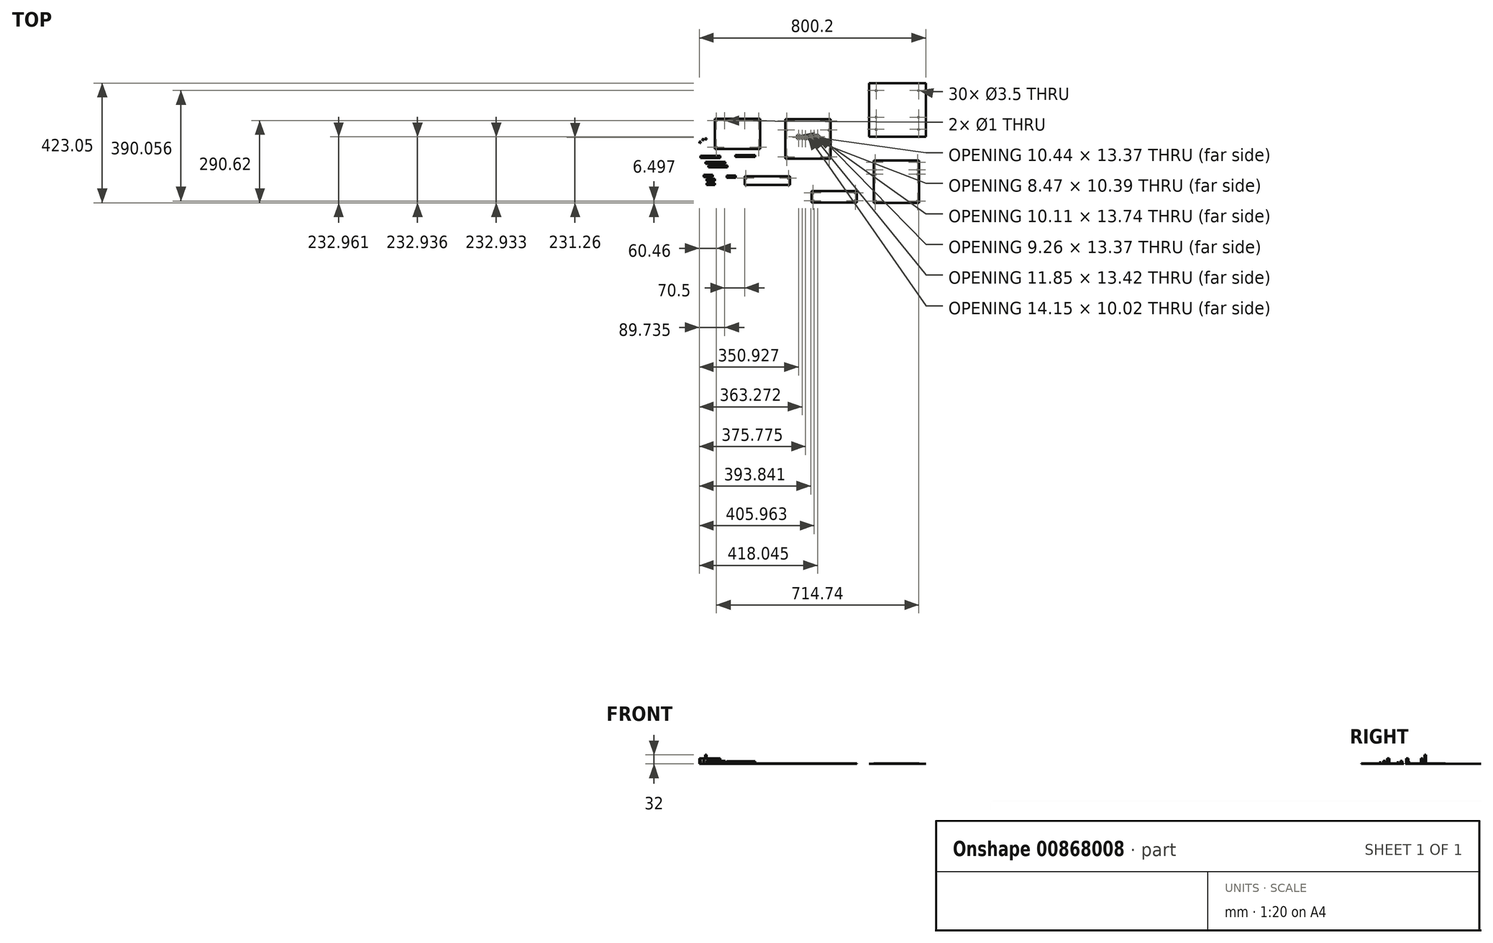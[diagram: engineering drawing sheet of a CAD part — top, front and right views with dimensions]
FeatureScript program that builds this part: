
annotation { "Feature Type Name" : "Feature", "Feature Type Description" : "" }
export const myFeature = defineFeature(function(context is Context, id is Id, definition is map)
    precondition{}
    {
        {
            var Q0;
            Q0=qCreatedBy(makeId("Top.planeOp"),FACE);
            var sketch = newSketch(context, id + "F0", { "sketchPlane" : qUnion([Q0])});
            skLineSegment(sketch, "E0.bottom", {"start": v(0, 0) * mm, "end": v(160, 0) * mm});
            skLineSegment(sketch, "E0.top", {"start": v(0, 107.5) * mm, "end": v(160, 107.5) * mm});
            skLineSegment(sketch, "E0.left", {"start": v(0, 0) * mm, "end": v(0, 107.5) * mm});
            skLineSegment(sketch, "E0.right", {"start": v(160, 0) * mm, "end": v(160, 107.5) * mm});
            skLineSegment(sketch, "E1", {"start": v(34.27, 115.15) * mm, "end": v(34.27, 89.45) * mm, "construction": true});
            skLineSegment(sketch, "E2", {"start": v(104.78, 115.15) * mm, "end": v(104.78, 86.57) * mm, "construction": true});
            skLineSegment(sketch, "E3.bottom", {"start": v(5, 101) * mm, "end": v(155, 101) * mm, "construction": true});
            skLineSegment(sketch, "E3.top", {"start": v(5, 6.5) * mm, "end": v(155, 6.5) * mm, "construction": true});
            skLineSegment(sketch, "E3.left", {"start": v(5, 101) * mm, "end": v(5, 6.5) * mm, "construction": true});
            skLineSegment(sketch, "E3.right", {"start": v(155, 101) * mm, "end": v(155, 6.5) * mm, "construction": true});
            skCircle(sketch, "E4", {"center": v(34.27, 101) * mm, "radius": 0.5 * mm});
            skCircle(sketch, "E5", {"center": v(104.78, 101) * mm, "radius": 0.5 * mm});
            skSolve(sketch);
        }
        {
            var Q0;
            Q0=makeQuery(id+"F0.imprint","IMPRINT",FACE,{"disambiguationData":[TD([[makeQuery(id+"F0.imprint","IMPRINT",EDGE,{"derivedFrom":sQuery(id+"F0.wireOp",EDGE,"E0.bottom")}),1.0]])]});
            extrude(context, id + "F1", {"entities" : qUnion([Q0]), "depth" : 1.6 * mm, "offsetDistance" : 25 * mm});
        }
        {
            var Q0;
            Q0=sQuery(id+"F0.wireOp",VERTEX,"E3.bottom.start");
            var Q1;
            Q1=sQuery(id+"F0.wireOp",VERTEX,"E3.bottom.end");
            var Q2;
            Q2=sQuery(id+"F0.wireOp",VERTEX,"E3.top.end");
            var Q3;
            Q3=sQuery(id+"F0.wireOp",VERTEX,"E3.top.start");
            var Q4;
            Q4=makeQuery(id+"F1.opExtrude","SWEPT_BODY",BODY,{"disambiguationData":[OSD([sQuery(id+"F0.wireOp",EDGE,"E0.bottom"),sQuery(id+"F0.wireOp",EDGE,"E0.top"),sQuery(id+"F0.wireOp",EDGE,"E0.left"),sQuery(id+"F0.wireOp",EDGE,"E0.right")])]});
            hole(context, id + "F2", {"style" : HoleStyle.SIMPLE, "endStyle" : HoleEndStyle.THROUGH, "oppositeDirection" : true, "holeDiameter" : 3.5 * mm, "majorDiameter" : 5 * mm, "isTappedThrough" : true, "tappedDepth" : 12 * mm, "tapClearance" : 3, "startFromSketch" : true, "locations" : qUnion([Q0, Q1, Q2, Q3]), "scope" : qUnion([Q4])});
        }
        {
            var Q0;
            Q0=qCreatedBy(makeId("Top.planeOp"),FACE);
            var sketch = newSketch(context, id + "F3", { "sketchPlane" : qUnion([Q0])});
            skLineSegment(sketch, "E6.bottom", {"start": v(-51.1, -23.64) * mm, "end": v(18.9, -23.64) * mm});
            skLineSegment(sketch, "E6.top", {"start": v(-51.1, -30.64) * mm, "end": v(18.9, -30.64) * mm});
            skLineSegment(sketch, "E6.left", {"start": v(-51.1, -23.64) * mm, "end": v(-51.1, -30.64) * mm});
            skLineSegment(sketch, "E6.right", {"start": v(18.9, -23.64) * mm, "end": v(18.9, -30.64) * mm});
            skSolve(sketch);
        }
        {
            var Q0;
            Q0=makeQuery(id+"F3.imprint","IMPRINT",FACE,{"disambiguationData":[TD([[makeQuery(id+"F3.imprint","IMPRINT",EDGE,{"derivedFrom":sQuery(id+"F3.wireOp",EDGE,"E6.bottom")}),-1.0]])]});
            extrude(context, id + "F4", {"entities" : qUnion([Q0]), "depth" : 20 * mm, "offsetDistance" : 25 * mm});
        }
        {
            var Q0;
            Q0=qCreatedBy(makeId("Top.planeOp"),FACE);
            var sketch = newSketch(context, id + "F5", { "sketchPlane" : qUnion([Q0])});
            skLineSegment(sketch, "E7.bottom", {"start": v(-33.26, -44.66) * mm, "end": v(36.74, -44.66) * mm});
            skLineSegment(sketch, "E7.top", {"start": v(-33.26, -51.66) * mm, "end": v(36.74, -51.66) * mm});
            skLineSegment(sketch, "E7.left", {"start": v(-33.26, -44.66) * mm, "end": v(-33.26, -51.66) * mm});
            skLineSegment(sketch, "E7.right", {"start": v(36.74, -44.66) * mm, "end": v(36.74, -51.66) * mm});
            skSolve(sketch);
        }
        {
            var Q0;
            Q0=makeQuery(id+"F5.imprint","IMPRINT",FACE,{"disambiguationData":[TD([[makeQuery(id+"F5.imprint","IMPRINT",EDGE,{"derivedFrom":sQuery(id+"F5.wireOp",EDGE,"E7.bottom")}),-1.0]])]});
            extrude(context, id + "F6", {"entities" : qUnion([Q0]), "depth" : 10.4 * mm, "offsetDistance" : 25 * mm});
        }
        {
            var Q0;
            Q0=qCreatedBy(makeId("Top.planeOp"),FACE);
            var sketch = newSketch(context, id + "F7", { "sketchPlane" : qUnion([Q0])});
            skLineSegment(sketch, "E8.bottom", {"start": v(-22.8, -58.18) * mm, "end": v(44.2, -58.18) * mm});
            skLineSegment(sketch, "E8.top", {"start": v(-22.8, -63.88) * mm, "end": v(44.2, -63.88) * mm});
            skLineSegment(sketch, "E8.left", {"start": v(-22.8, -58.18) * mm, "end": v(-22.8, -63.88) * mm});
            skLineSegment(sketch, "E8.right", {"start": v(44.2, -58.18) * mm, "end": v(44.2, -63.88) * mm});
            skSolve(sketch);
        }
        {
            var Q0;
            Q0=makeQuery(id+"F7.imprint","IMPRINT",FACE,{"disambiguationData":[TD([[makeQuery(id+"F7.imprint","IMPRINT",EDGE,{"derivedFrom":sQuery(id+"F7.wireOp",EDGE,"E8.bottom")}),-1.0]])]});
            extrude(context, id + "F8", {"entities" : qUnion([Q0]), "depth" : 5.5 * mm, "offsetDistance" : 25 * mm});
        }
        {
            var Q0;
            Q0=qCreatedBy(makeId("Top.planeOp"),FACE);
            var sketch = newSketch(context, id + "F9", { "sketchPlane" : qUnion([Q0])});
            skLineSegment(sketch, "E9.bottom", {"start": v(72.56, -20.42) * mm, "end": v(142.56, -20.42) * mm});
            skLineSegment(sketch, "E9.top", {"start": v(72.56, -27.42) * mm, "end": v(142.56, -27.42) * mm});
            skLineSegment(sketch, "E9.left", {"start": v(72.56, -20.42) * mm, "end": v(72.56, -27.42) * mm});
            skLineSegment(sketch, "E9.right", {"start": v(142.56, -20.42) * mm, "end": v(142.56, -27.42) * mm});
            skSolve(sketch);
        }
        {
            var Q0;
            Q0=makeQuery(id+"F9.imprint","IMPRINT",FACE,{"disambiguationData":[TD([[makeQuery(id+"F9.imprint","IMPRINT",EDGE,{"derivedFrom":sQuery(id+"F9.wireOp",EDGE,"E9.bottom")}),-1.0]])]});
            extrude(context, id + "F10", {"entities" : qUnion([Q0]), "depth" : 9.8 * mm, "offsetDistance" : 25 * mm});
        }
        {
            var Q0;
            Q0=qCreatedBy(makeId("Top.planeOp"),FACE);
            var sketch = newSketch(context, id + "F11", { "sketchPlane" : qUnion([Q0])});
            skLineSegment(sketch, "E10.bottom", {"start": v(-40, -91.42) * mm, "end": v(-8, -91.42) * mm});
            skLineSegment(sketch, "E10.top", {"start": v(-40, -98.42) * mm, "end": v(-8, -98.42) * mm});
            skLineSegment(sketch, "E10.left", {"start": v(-40, -91.42) * mm, "end": v(-40, -98.42) * mm});
            skLineSegment(sketch, "E10.right", {"start": v(-8, -91.42) * mm, "end": v(-8, -98.42) * mm});
            skSolve(sketch);
        }
        {
            var Q0;
            Q0=makeQuery(id+"F11.imprint","IMPRINT",FACE,{"disambiguationData":[TD([[makeQuery(id+"F11.imprint","IMPRINT",EDGE,{"derivedFrom":sQuery(id+"F11.wireOp",EDGE,"E10.bottom")}),-1.0]])]});
            extrude(context, id + "F12", {"entities" : qUnion([Q0]), "depth" : 20 * mm, "offsetDistance" : 25 * mm});
        }
        {
            var Q0;
            Q0=qCreatedBy(makeId("Top.planeOp"),FACE);
            var sketch = newSketch(context, id + "F13", { "sketchPlane" : qUnion([Q0])});
            skLineSegment(sketch, "E11.bottom", {"start": v(-30, -105.14) * mm, "end": v(0, -105.14) * mm});
            skLineSegment(sketch, "E11.top", {"start": v(-30, -112.14) * mm, "end": v(0, -112.14) * mm});
            skLineSegment(sketch, "E11.left", {"start": v(-30, -105.14) * mm, "end": v(-30, -112.14) * mm});
            skLineSegment(sketch, "E11.right", {"start": v(0, -105.14) * mm, "end": v(0, -112.14) * mm});
            skSolve(sketch);
        }
        {
            var Q0;
            Q0=makeQuery(id+"F13.imprint","IMPRINT",FACE,{"disambiguationData":[TD([[makeQuery(id+"F13.imprint","IMPRINT",EDGE,{"derivedFrom":sQuery(id+"F13.wireOp",EDGE,"E11.bottom")}),-1.0]])]});
            extrude(context, id + "F14", {"entities" : qUnion([Q0]), "depth" : 10.4 * mm, "offsetDistance" : 25 * mm});
        }
        {
            var Q0;
            Q0=qCreatedBy(makeId("Top.planeOp"),FACE);
            var sketch = newSketch(context, id + "F15", { "sketchPlane" : qUnion([Q0])});
            skLineSegment(sketch, "E12.bottom", {"start": v(-29, -120.64) * mm, "end": v(0, -120.64) * mm});
            skLineSegment(sketch, "E12.top", {"start": v(-29, -126.34) * mm, "end": v(0, -126.34) * mm});
            skLineSegment(sketch, "E12.left", {"start": v(-29, -120.64) * mm, "end": v(-29, -126.34) * mm});
            skLineSegment(sketch, "E12.right", {"start": v(0, -120.64) * mm, "end": v(0, -126.34) * mm});
            skSolve(sketch);
        }
        {
            var Q0;
            Q0=makeQuery(id+"F15.imprint","IMPRINT",FACE,{"disambiguationData":[TD([[makeQuery(id+"F15.imprint","IMPRINT",EDGE,{"derivedFrom":sQuery(id+"F15.wireOp",EDGE,"E12.bottom")}),-1.0]])]});
            extrude(context, id + "F16", {"entities" : qUnion([Q0]), "depth" : 5.5 * mm, "offsetDistance" : 25 * mm});
        }
        {
            var Q0;
            Q0=qCreatedBy(makeId("Top.planeOp"),FACE);
            var sketch = newSketch(context, id + "F17", { "sketchPlane" : qUnion([Q0])});
            skLineSegment(sketch, "E13.bottom", {"start": v(41.03, -93.71) * mm, "end": v(73.03, -93.71) * mm});
            skLineSegment(sketch, "E13.top", {"start": v(41.03, -100.71) * mm, "end": v(73.03, -100.71) * mm});
            skLineSegment(sketch, "E13.left", {"start": v(41.03, -93.71) * mm, "end": v(41.03, -100.71) * mm});
            skLineSegment(sketch, "E13.right", {"start": v(73.03, -93.71) * mm, "end": v(73.03, -100.71) * mm});
            skSolve(sketch);
        }
        {
            var Q0;
            Q0=makeQuery(id+"F17.imprint","IMPRINT",FACE,{"disambiguationData":[TD([[makeQuery(id+"F17.imprint","IMPRINT",EDGE,{"derivedFrom":sQuery(id+"F17.wireOp",EDGE,"E13.bottom")}),-1.0]])]});
            extrude(context, id + "F18", {"entities" : qUnion([Q0]), "depth" : 9.8 * mm, "offsetDistance" : 25 * mm});
        }
        {
            var Q0;
            Q0=qCreatedBy(makeId("Top.planeOp"),FACE);
            var sketch = newSketch(context, id + "F19", { "sketchPlane" : qUnion([Q0])});
            skCircle(sketch, "E14.cCircle", {"center": v(-52.9, 24.26) * mm, "radius": 2.5 * mm, "construction": true});
            skLineSegment(sketch, "E14.0", {"start": v(-52.82, 27.15) * mm, "end": v(-50.36, 25.63) * mm});
            skLineSegment(sketch, "E14.1", {"start": v(-50.36, 25.63) * mm, "end": v(-50.46, 22.74) * mm});
            skLineSegment(sketch, "E14.2", {"start": v(-50.46, 22.74) * mm, "end": v(-53, 21.38) * mm});
            skLineSegment(sketch, "E14.3", {"start": v(-53, 21.38) * mm, "end": v(-55.46, 22.9) * mm});
            skLineSegment(sketch, "E14.4", {"start": v(-55.46, 22.9) * mm, "end": v(-55.36, 25.79) * mm});
            skLineSegment(sketch, "E14.5", {"start": v(-55.36, 25.79) * mm, "end": v(-52.82, 27.15) * mm});
            skPoint(sketch, "E14.0.midPoint", {"position": v(-51.59, 26.39) * mm});
            skSolve(sketch);
        }
        {
            var Q0;
            Q0=makeQuery(id+"F19.imprint","IMPRINT",FACE,{"disambiguationData":[TD([[makeQuery(id+"F19.imprint","IMPRINT",EDGE,{"derivedFrom":sQuery(id+"F19.wireOp",EDGE,"E14.0")}),-1.0]])]});
            extrude(context, id + "F20", {"entities" : qUnion([Q0]), "depth" : 20 * mm, "offsetDistance" : 25 * mm});
        }
        {
            var Q0;
            Q0=qCreatedBy(makeId("Top.planeOp"),FACE);
            var sketch = newSketch(context, id + "F21", { "sketchPlane" : qUnion([Q0])});
            skLineSegment(sketch, "E15.bottom", {"start": v(104.6, -96.45) * mm, "end": v(264.6, -96.45) * mm});
            skLineSegment(sketch, "E15.top", {"start": v(104.6, -126.45) * mm, "end": v(264.6, -126.45) * mm});
            skLineSegment(sketch, "E15.left", {"start": v(104.6, -96.45) * mm, "end": v(104.6, -126.45) * mm});
            skLineSegment(sketch, "E15.right", {"start": v(264.6, -96.45) * mm, "end": v(264.6, -126.45) * mm});
            skCircle(sketch, "E16", {"center": v(109.6, -102.95) * mm, "radius": 1.75 * mm});
            skCircle(sketch, "E17", {"center": v(259.6, -102.95) * mm, "radius": 1.75 * mm});
            skSolve(sketch);
        }
        {
            var Q0;
            Q0=makeQuery(id+"F21.imprint","IMPRINT",FACE,{"disambiguationData":[TD([[makeQuery(id+"F21.imprint","IMPRINT",EDGE,{"derivedFrom":sQuery(id+"F21.wireOp",EDGE,"E15.bottom")}),-1.0]])]});
            extrude(context, id + "F22", {"entities" : qUnion([Q0]), "depth" : 1.6 * mm, "offsetDistance" : 25 * mm});
        }
        {
            var Q0;
            Q0=qCreatedBy(makeId("Top.planeOp"),FACE);
            var sketch = newSketch(context, id + "F23", { "sketchPlane" : qUnion([Q0])});
            skLineSegment(sketch, "E18.bottom", {"start": v(248.41, 106.6) * mm, "end": v(408.41, 106.6) * mm});
            skLineSegment(sketch, "E18.top", {"start": v(248.41, -33.4) * mm, "end": v(408.41, -33.4) * mm});
            skLineSegment(sketch, "E18.left", {"start": v(248.41, 106.6) * mm, "end": v(248.41, -33.4) * mm});
            skLineSegment(sketch, "E18.right", {"start": v(408.41, 106.6) * mm, "end": v(408.41, -33.4) * mm});
            skCircle(sketch, "E19", {"center": v(253.41, 100.1) * mm, "radius": 1.75 * mm});
            skCircle(sketch, "E20", {"center": v(403.41, 100.1) * mm, "radius": 1.75 * mm});
            skCircle(sketch, "E21", {"center": v(253.41, 67.6) * mm, "radius": 1.75 * mm});
            skCircle(sketch, "E22", {"center": v(403.41, 67.6) * mm, "radius": 1.75 * mm});
            skCircle(sketch, "E23", {"center": v(253.41, -26.9) * mm, "radius": 1.75 * mm});
            skCircle(sketch, "E24", {"center": v(403.41, -26.9) * mm, "radius": 1.75 * mm});
            skText(sketch, "E25", { "text": "New ACB", "fontName": "OpenSans-Regular.ttf"});
            const initialGuessF23  = {"E25": [0.28841, 0.03663, 1, 0, 0.01348]};
            skSetInitialGuess(sketch, initialGuessF23);
            skSolve(sketch);
        }
        {
            var Q0;
            Q0=makeQuery(id+"F23.imprint","IMPRINT",FACE,{"disambiguationData":[TD([[makeQuery(id+"F23.imprint","IMPRINT",EDGE,{"derivedFrom":sQuery(id+"F23.wireOp",EDGE,"E18.bottom")}),-1.0]])]});
            extrude(context, id + "F24", {"entities" : qUnion([Q0]), "depth" : 1.6 * mm, "offsetDistance" : 25 * mm});
        }
        {
            var Q0;
            Q0=qCreatedBy(makeId("Top.planeOp"),FACE);
            var sketch = newSketch(context, id + "F25", { "sketchPlane" : qUnion([Q0])});
            skCircle(sketch, "E26.cCircle", {"center": v(-41.73, 33.8) * mm, "radius": 2.5 * mm, "construction": true});
            skLineSegment(sketch, "E26.0", {"start": v(-39.25, 32.34) * mm, "end": v(-41.76, 30.91) * mm});
            skLineSegment(sketch, "E26.1", {"start": v(-41.76, 30.91) * mm, "end": v(-44.25, 32.38) * mm});
            skLineSegment(sketch, "E26.2", {"start": v(-44.25, 32.38) * mm, "end": v(-44.22, 35.26) * mm});
            skLineSegment(sketch, "E26.3", {"start": v(-44.22, 35.26) * mm, "end": v(-41.71, 36.69) * mm});
            skLineSegment(sketch, "E26.4", {"start": v(-41.71, 36.69) * mm, "end": v(-39.22, 35.22) * mm});
            skLineSegment(sketch, "E26.5", {"start": v(-39.22, 35.22) * mm, "end": v(-39.25, 32.34) * mm});
            skPoint(sketch, "E26.0.midPoint", {"position": v(-40.5, 31.63) * mm});
            skSolve(sketch);
        }
        {
            var Q0;
            Q0=makeQuery(id+"F25.imprint","IMPRINT",FACE,{"disambiguationData":[TD([[makeQuery(id+"F25.imprint","IMPRINT",EDGE,{"derivedFrom":sQuery(id+"F25.wireOp",EDGE,"E26.0")}),-1.0]])]});
            extrude(context, id + "F26", {"entities" : qUnion([Q0]), "depth" : 10 * mm, "offsetDistance" : 25 * mm});
        }
        {
            var Q0;
            Q0=qCreatedBy(makeId("Top.planeOp"),FACE);
            var sketch = newSketch(context, id + "F27", { "sketchPlane" : qUnion([Q0])});
            skCircle(sketch, "E27.cCircle", {"center": v(-32.14, 35.9) * mm, "radius": 2.5 * mm, "construction": true});
            skLineSegment(sketch, "E27.0", {"start": v(-29.63, 34.48) * mm, "end": v(-32.12, 33.02) * mm});
            skLineSegment(sketch, "E27.1", {"start": v(-32.12, 33.02) * mm, "end": v(-34.63, 34.45) * mm});
            skLineSegment(sketch, "E27.2", {"start": v(-34.63, 34.45) * mm, "end": v(-34.65, 37.33) * mm});
            skLineSegment(sketch, "E27.3", {"start": v(-34.65, 37.33) * mm, "end": v(-32.15, 38.8) * mm});
            skLineSegment(sketch, "E27.4", {"start": v(-32.15, 38.8) * mm, "end": v(-29.65, 37.36) * mm});
            skLineSegment(sketch, "E27.5", {"start": v(-29.65, 37.36) * mm, "end": v(-29.63, 34.48) * mm});
            skPoint(sketch, "E27.0.midPoint", {"position": v(-30.88, 33.75) * mm});
            skSolve(sketch);
        }
        {
            var Q0;
            Q0=makeQuery(id+"F27.imprint","IMPRINT",FACE,{"disambiguationData":[TD([[makeQuery(id+"F27.imprint","IMPRINT",EDGE,{"derivedFrom":sQuery(id+"F27.wireOp",EDGE,"E27.0")}),-1.0]])]});
            extrude(context, id + "F28", {"entities" : qUnion([Q0]), "depth" : 32 * mm, "offsetDistance" : 25 * mm});
        }
        {
            var Q0;
            Q0=qCreatedBy(makeId("Top.planeOp"),FACE);
            var sketch = newSketch(context, id + "F29", { "sketchPlane" : qUnion([Q0])});
            skLineSegment(sketch, "E28.bottom", {"start": v(341.16, -148.37) * mm, "end": v(501.16, -148.37) * mm});
            skLineSegment(sketch, "E28.top", {"start": v(341.16, -188.37) * mm, "end": v(501.16, -188.37) * mm});
            skLineSegment(sketch, "E28.left", {"start": v(341.16, -148.37) * mm, "end": v(341.16, -188.37) * mm});
            skLineSegment(sketch, "E28.right", {"start": v(501.16, -148.37) * mm, "end": v(501.16, -188.37) * mm});
            skCircle(sketch, "E29", {"center": v(346.16, -154.87) * mm, "radius": 1.75 * mm});
            skCircle(sketch, "E30", {"center": v(346.16, -181.87) * mm, "radius": 1.75 * mm});
            skCircle(sketch, "E31", {"center": v(496.16, -154.87) * mm, "radius": 1.75 * mm});
            skCircle(sketch, "E32", {"center": v(496.16, -181.87) * mm, "radius": 1.75 * mm});
            skSolve(sketch);
        }
        {
            var Q0;
            Q0=qCreatedBy(makeId("Top.planeOp"),FACE);
            var sketch = newSketch(context, id + "F30", { "sketchPlane" : qUnion([Q0])});
            skLineSegment(sketch, "E33.bottom", {"start": v(561.3, -39.62) * mm, "end": v(721.3, -39.62) * mm});
            skLineSegment(sketch, "E33.top", {"start": v(561.3, -189.62) * mm, "end": v(721.3, -189.62) * mm});
            skLineSegment(sketch, "E33.left", {"start": v(561.3, -39.62) * mm, "end": v(561.3, -189.62) * mm});
            skLineSegment(sketch, "E33.right", {"start": v(721.3, -39.62) * mm, "end": v(721.3, -189.62) * mm});
            skCircle(sketch, "E34", {"center": v(566.3, -183.12) * mm, "radius": 1.75 * mm});
            skCircle(sketch, "E35", {"center": v(716.3, -183.12) * mm, "radius": 1.75 * mm});
            skCircle(sketch, "E36", {"center": v(566.3, -88.62) * mm, "radius": 1.75 * mm});
            skCircle(sketch, "E37", {"center": v(716.3, -88.62) * mm, "radius": 1.75 * mm});
            skCircle(sketch, "E38", {"center": v(566.3, -73.12) * mm, "radius": 1.75 * mm});
            skCircle(sketch, "E39", {"center": v(716.3, -73.12) * mm, "radius": 1.75 * mm});
            skCircle(sketch, "E40", {"center": v(716.3, -46.12) * mm, "radius": 1.75 * mm});
            skCircle(sketch, "E41", {"center": v(566.3, -46.12) * mm, "radius": 1.75 * mm});
            skSolve(sketch);
        }
        {
            var Q0;
            Q0=makeQuery(id+"F29.imprint","IMPRINT",FACE,{"disambiguationData":[TD([[makeQuery(id+"F29.imprint","IMPRINT",EDGE,{"derivedFrom":sQuery(id+"F29.wireOp",EDGE,"E28.bottom")}),-1.0]])]});
            extrude(context, id + "F31", {"entities" : qUnion([Q0]), "depth" : 1.6 * mm, "offsetDistance" : 25 * mm});
        }
        {
            var Q0;
            Q0=makeQuery(id+"F30.imprint","IMPRINT",FACE,{"disambiguationData":[TD([[makeQuery(id+"F30.imprint","IMPRINT",EDGE,{"derivedFrom":sQuery(id+"F30.wireOp",EDGE,"E33.bottom")}),-1.0]])]});
            extrude(context, id + "F32", {"entities" : qUnion([Q0]), "depth" : 1.6 * mm, "offsetDistance" : 25 * mm});
        }
        {
            var Q0;
            Q0=qCreatedBy(makeId("Top.planeOp"),FACE);
            var sketch = newSketch(context, id + "F33", { "sketchPlane" : qUnion([Q0])});
            skLineSegment(sketch, "E42.bottom", {"start": v(544.74, 233.43) * mm, "end": v(744.74, 233.43) * mm});
            skLineSegment(sketch, "E42.top", {"start": v(544.74, 43.43) * mm, "end": v(744.74, 43.43) * mm});
            skLineSegment(sketch, "E42.left", {"start": v(544.74, 233.43) * mm, "end": v(544.74, 43.43) * mm});
            skLineSegment(sketch, "E42.right", {"start": v(744.74, 233.43) * mm, "end": v(744.74, 43.43) * mm});
            skSolve(sketch);
        }
        {
            var Q0;
            Q0=makeQuery(id+"F33.imprint","IMPRINT",FACE,{"disambiguationData":[TD([[makeQuery(id+"F33.imprint","IMPRINT",EDGE,{"derivedFrom":sQuery(id+"F33.wireOp",EDGE,"E42.bottom")}),-1.0]])]});
            extrude(context, id + "F34", {"entities" : qUnion([Q0]), "depth" : 0.1 * mm, "offsetDistance" : 25 * mm});
        }
        {
            var Q0;
            Q0=makeQuery(id+"F34.opExtrude","CAP_FACE",FACE,{"disambiguationData":[OSD([sQuery(id+"F33.wireOp",EDGE,"E42.bottom"),sQuery(id+"F33.wireOp",EDGE,"E42.top"),sQuery(id+"F33.wireOp",EDGE,"E42.left"),sQuery(id+"F33.wireOp",EDGE,"E42.right")])],"isStart":false});
            var sketch = newSketch(context, id + "F35", { "sketchPlane" : qUnion([Q0])});
            skCircle(sketch, "E43", {"center": v(569.74, 206.93) * mm, "radius": 1.75 * mm});
            skCircle(sketch, "E44", {"center": v(569.74, 69.93) * mm, "radius": 1.75 * mm});
            skCircle(sketch, "E45", {"center": v(719.74, 206.93) * mm, "radius": 1.75 * mm});
            skCircle(sketch, "E46", {"center": v(719.74, 69.93) * mm, "radius": 1.75 * mm});
            skCircle(sketch, "E47", {"center": v(569.74, 112.43) * mm, "radius": 1.75 * mm});
            skCircle(sketch, "E48", {"center": v(719.74, 112.43) * mm, "radius": 1.75 * mm});
            skSolve(sketch);
        }
        {
            var Q0;
            Q0=sQuery(id+"F35.wireOp",VERTEX,"E45.center");
            var Q1;
            Q1=sQuery(id+"F35.wireOp",VERTEX,"E43.center");
            var Q2;
            Q2=sQuery(id+"F35.wireOp",VERTEX,"E47.center");
            var Q3;
            Q3=sQuery(id+"F35.wireOp",VERTEX,"E48.center");
            var Q4;
            Q4=sQuery(id+"F35.wireOp",VERTEX,"E46.center");
            var Q5;
            Q5=sQuery(id+"F35.wireOp",VERTEX,"E44.center");
            var Q6;
            Q6=makeQuery(id+"F34.opExtrude","SWEPT_BODY",BODY,{"disambiguationData":[OSD([sQuery(id+"F33.wireOp",EDGE,"E42.bottom"),sQuery(id+"F33.wireOp",EDGE,"E42.top"),sQuery(id+"F33.wireOp",EDGE,"E42.left"),sQuery(id+"F33.wireOp",EDGE,"E42.right")])]});
            hole(context, id + "F36", {"style" : HoleStyle.SIMPLE, "endStyle" : HoleEndStyle.THROUGH, "holeDiameter" : 3.5 * mm, "majorDiameter" : 5 * mm, "isTappedThrough" : true, "tappedDepth" : 12 * mm, "tapClearance" : 3, "startFromSketch" : true, "locations" : qUnion([Q0, Q1, Q2, Q3, Q4, Q5]), "scope" : qUnion([Q6])});
        }
    });
